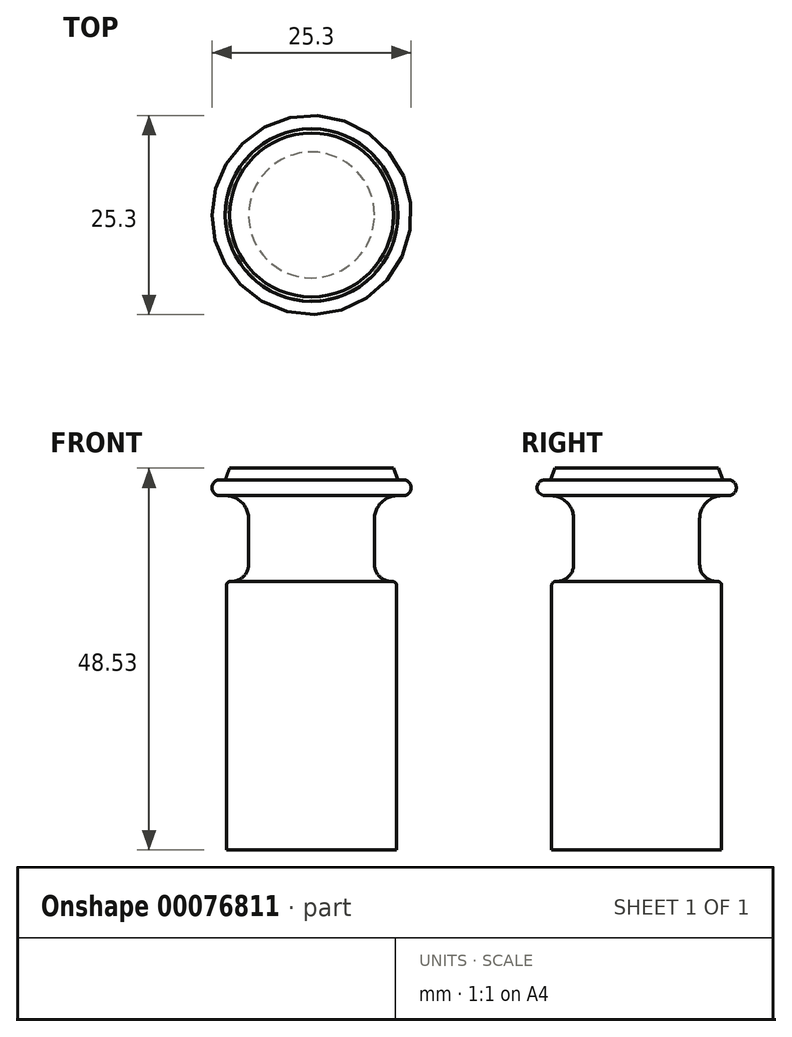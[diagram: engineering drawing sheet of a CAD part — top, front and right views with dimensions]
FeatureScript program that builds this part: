
annotation { "Feature Type Name" : "Feature", "Feature Type Description" : "" }
export const myFeature = defineFeature(function(context is Context, id is Id, definition is map)
    precondition{}
    {
        {
            var Q0;
            Q0=qCreatedBy(makeId("Front.planeOp"),FACE);
            var sketch = newSketch(context, id + "F0", { "sketchPlane" : qUnion([Q0])});
            skLineSegment(sketch, "E0", {"start": v(0, 0) * mm, "end": v(0, 48.53) * mm});
            skLineSegment(sketch, "E1", {"start": v(0, 48.53) * mm, "end": v(10.4, 48.53) * mm});
            skLineSegment(sketch, "E2", {"start": v(10.4, 48.53) * mm, "end": v(10.96, 47.03) * mm});
            skLineSegment(sketch, "E3", {"start": v(10.96, 47.03) * mm, "end": v(11.65, 47.03) * mm});
            skLineSegment(sketch, "E4", {"start": v(12.65, 46.03) * mm, "end": v(12.65, 46.03) * mm});
            skLineSegment(sketch, "E5", {"start": v(11.65, 45.03) * mm, "end": v(10.94, 45.03) * mm});
            skLineSegment(sketch, "E6", {"start": v(8, 42.09) * mm, "end": v(8, 36.3) * mm});
            skLineSegment(sketch, "E7", {"start": v(10.17, 34.12) * mm, "end": v(10.3, 34.12) * mm});
            skLineSegment(sketch, "E8", {"start": v(10.8, 33.62) * mm, "end": v(10.8, 0) * mm});
            skPoint(sketch, "E9.visualSharp", {"position": v(8, 34.12) * mm});
            skArc(sketch, "E9.filletArc", {"start": v(8, 36.3) * mm, "mid": v(8.63, 34.76) * mm, "end": v(10.17, 34.12) * mm});
            skPoint(sketch, "E10.visualSharp", {"position": v(8, 45.03) * mm});
            skArc(sketch, "E10.filletArc", {"start": v(10.94, 45.03) * mm, "mid": v(8.86, 44.17) * mm, "end": v(8, 42.09) * mm});
            skPoint(sketch, "E11.visualSharp", {"position": v(12.65, 47.03) * mm});
            skArc(sketch, "E11.filletArc", {"start": v(12.65, 46.03) * mm, "mid": v(12.36, 46.74) * mm, "end": v(11.65, 47.03) * mm});
            skPoint(sketch, "E12.visualSharp", {"position": v(12.65, 45.03) * mm});
            skArc(sketch, "E12.filletArc", {"start": v(11.65, 45.03) * mm, "mid": v(12.36, 45.33) * mm, "end": v(12.65, 46.03) * mm});
            skPoint(sketch, "E13.visualSharp", {"position": v(10.8, 34.12) * mm});
            skArc(sketch, "E13.filletArc", {"start": v(10.8, 33.62) * mm, "mid": v(10.65, 33.98) * mm, "end": v(10.3, 34.12) * mm});
            skLineSegment(sketch, "E14", {"start": v(0, 0) * mm, "end": v(10.8, 0) * mm});
            skSolve(sketch);
        }
        {
            var Q0;
            Q0=qCreatedBy(makeId("Front.planeOp"),FACE);
            var sketch = newSketch(context, id + "F1", { "sketchPlane" : qUnion([Q0])});
            skLineSegment(sketch, "E15", {"start": v(0, 58.08) * mm, "end": v(0, 67.2) * mm, "construction": true});
            skSolve(sketch);
        }
        {
            var Q0;
            Q0 = qSketchRegion(id + "F0", true);
            var Q1;
            Q1=sQuery(id+"F1.wireOp",EDGE,"E15");
            revolve(context, id + "F2", {"entities" : qUnion([Q0]), "axis" : qUnion([Q1]), "revolveType" : RevolveType.FULL});
        }
    });
